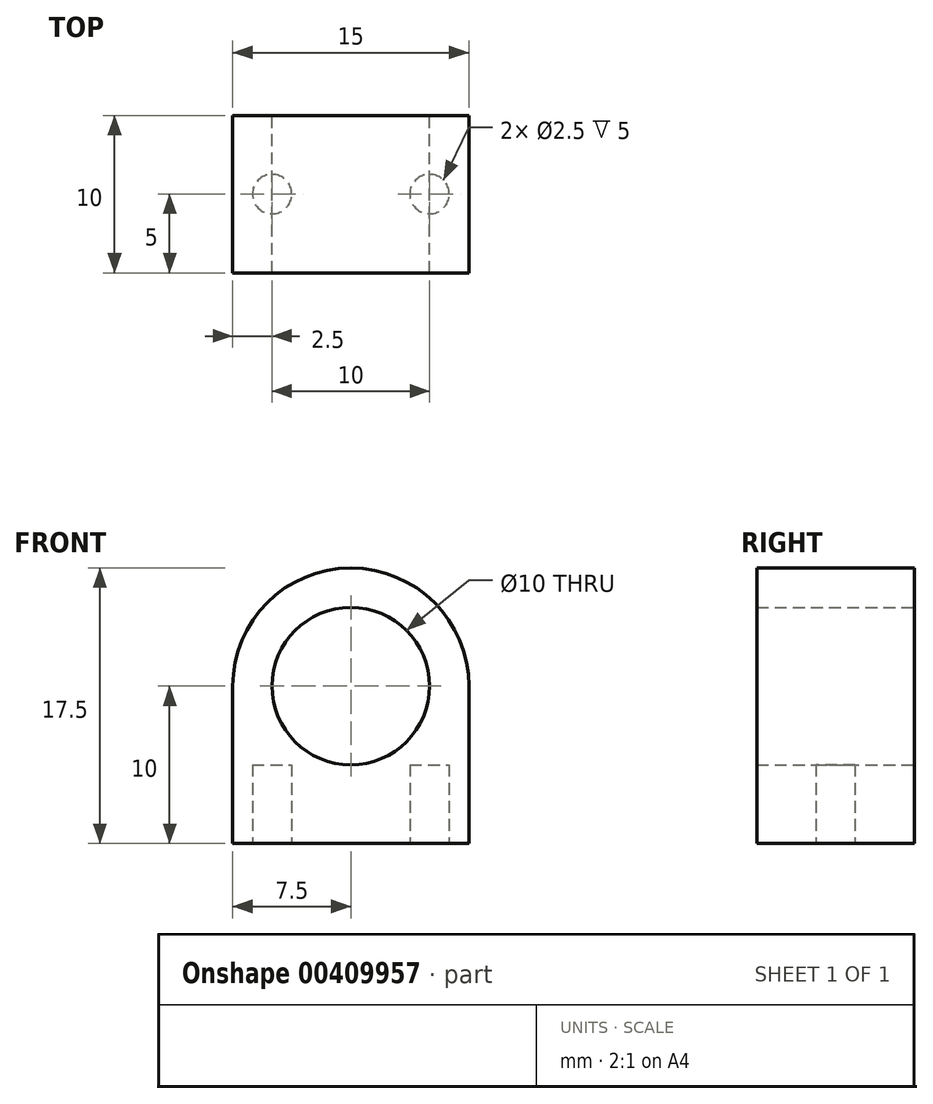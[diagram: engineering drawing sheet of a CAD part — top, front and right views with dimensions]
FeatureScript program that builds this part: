
annotation { "Feature Type Name" : "Feature", "Feature Type Description" : "" }
export const myFeature = defineFeature(function(context is Context, id is Id, definition is map)
    precondition{}
    {
        {
            var Q0;
            Q0=qCreatedBy(makeId("Front.planeOp"),FACE);
            var sketch = newSketch(context, id + "F0", { "sketchPlane" : qUnion([Q0])});
            skLineSegment(sketch, "E0", {"start": v(0, 0) * mm, "end": v(15, 0) * mm});
            skLineSegment(sketch, "E1", {"start": v(15, 0) * mm, "end": v(15, 10) * mm});
            skLineSegment(sketch, "E2", {"start": v(0, 10) * mm, "end": v(0, 0) * mm});
            skArc(sketch, "E3", {"start": v(15, 10) * mm, "mid": v(7.5, 17.5) * mm, "end": v(0, 10) * mm});
            skCircle(sketch, "E4", {"center": v(7.5, 10) * mm, "radius": 5 * mm});
            skSolve(sketch);
        }
        {
            var Q0;
            Q0 = qSketchRegion(id + "F0", true);
            extrude(context, id + "F1", {"entities" : qUnion([Q0]), "depth" : 10 * mm});
        }
        {
            var Q0;
            Q0=makeQuery(id+"F1.opExtrude","SWEPT_FACE",FACE,{"disambiguationData":[OSD([sQuery(id+"F0.wireOp",EDGE,"E0")])]});
            var sketch = newSketch(context, id + "F2", { "sketchPlane" : qUnion([Q0])});
            skCircle(sketch, "E5", {"center": v(2.5, 5) * mm, "radius": 1.25 * mm});
            skPoint(sketch, "E5.centerSnap0", {"position": v(0, 5) * mm});
            skCircle(sketch, "E6", {"center": v(12.5, 5) * mm, "radius": 1.25 * mm});
            skSolve(sketch);
        }
        {
            var Q0;
            Q0 = qSketchRegion(id + "F2", true);
            extrude(context, id + "F3", {"entities" : qUnion([Q0]), "operationType" : NewBodyOperationType.REMOVE, "oppositeDirection" : true, "depth" : 5 * mm});
        }
    });
